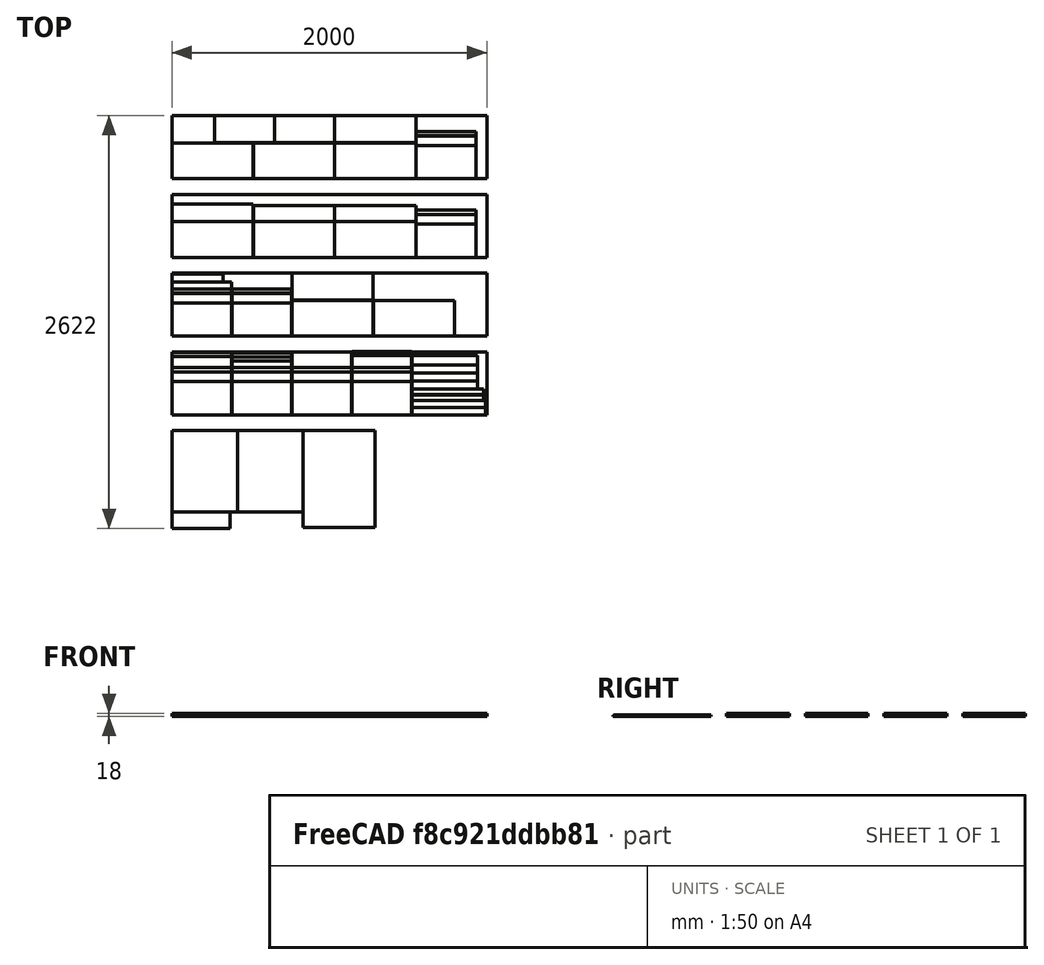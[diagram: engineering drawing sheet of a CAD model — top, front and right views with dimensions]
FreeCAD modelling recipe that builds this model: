
FCSTD DOCUMENT  (FreeCAD 0.16R)
Label: Schnittplan
License: All rights reserved
LicenseURL: http://en.wikipedia.org/wiki/All_rights_reserved
objects: Part::Box×66, App::DocumentObjectGroup×23
note: 66 computed .brp shape members not serialized (recipe doc carries the construction recipe); baked Part::Feature solids carry a one-line shape summary decoded from their .brp

FEATURE [Part::Box] Box  label="BRETT"
  Height = 18
  Length = 2000
  Width = 400
FEATURE [Part::Box] Box001  label="Dach Front Big"
  Height = 18
  Length = 380
  Placement = pos=(0,300,0) rot=(0,0,1;0rad)
  Width = 70
FEATURE [Part::Box] Box002  label="Dach Back small"
  Height = 18
  Length = 380
  Placement = pos=(381,300,0) rot=(0,0,1;0rad)
  Width = 40
FEATURE [Part::Box] Box003  label="Zarge Back outer upper"
  Height = 18
  Length = 380
  Placement = pos=(1143,211,0) rot=(0,0,1;0rad)
  Width = 60
FEATURE [Part::Box] Box004  label="Zarge Back outer lower "
  Height = 18
  Length = 380
  Placement = pos=(1143,272,0) rot=(0,0,1;0rad)
  Width = 27
FEATURE [Part::Box] Box005  label="Zarge Front inner"
  Height = 18
  Length = 380
  Placement = pos=(1143,0,0) rot=(0,0,1;0rad)
  Width = 210
FEATURE [Part::Box] Box007  label="Zarge Front outer lower"
  Height = 18
  Length = 380
  Placement = pos=(762,272,0) rot=(0,0,1;0rad)
  Width = 27
FEATURE [Part::Box] Box008  label="Zarge Back inner"
  Height = 18
  Length = 380
  Placement = pos=(762,0,0) rot=(0,0,1;0rad)
  Width = 210
FEATURE [Part::Box] Box006  label="Zarge Front outer upper"
  Height = 18
  Length = 380
  Placement = pos=(762,211,0) rot=(0,0,1;0rad)
  Width = 60
FEATURE [Part::Box] Box009  label="Boden Back with Hole"
  Height = 18
  Length = 380
  Placement = pos=(762,300,0) rot=(0,0,1;0rad)
  Width = 100
FEATURE [Part::Box] Box010  label="Boden Flogloch outer upper"
  Height = 18
  Length = 380
  Placement = pos=(1143,300,0) rot=(0,0,1;0rad)
  Width = 75
FEATURE [Part::Box] Box014  label="Zarge Front outer lower001"
  Height = 18
  Length = 380
  Placement = pos=(0,272,0) rot=(0,0,1;0rad)
  Width = 27
FEATURE [Part::Box] Box015  label="Zarge Back inner001"
  Height = 18
  Length = 380
  Placement = pos=(381,0,0) rot=(0,0,1;0rad)
  Width = 210
FEATURE [Part::Box] Box016  label="Zarge Front outer upper001"
  Height = 18
  Length = 380
  Placement = pos=(0,211,0) rot=(0,0,1;0rad)
  Width = 60
FEATURE [Part::Box] Box012  label="Zarge Back outer lower 001"
  Height = 18
  Length = 380
  Placement = pos=(381,272,0) rot=(0,0,1;0rad)
  Width = 27
FEATURE [Part::Box] Box013  label="Zarge Front inner001"
  Height = 18
  Length = 380
  Width = 210
FEATURE [Part::Box] Box017  label="Boden Fluglochverschluss"
  Height = 18
  Length = 380
  Placement = pos=(381,367,0) rot=(0,0,1;0rad)
  Width = 25
FEATURE [Part::Box] Box018  label="Boden Fluglochverschluss001"
  Height = 18
  Length = 380
  Placement = pos=(381,341,0) rot=(0,0,1;0rad)
  Width = 25
FEATURE [Part::Box] Box019  label="Boden Fluglochverschluss002"
  Height = 18
  Length = 380
  Placement = pos=(0,371,0) rot=(0,0,1;0rad)
  Width = 25
FEATURE [Part::Box] Box011  label="Zarge Back outer upper001"
  Height = 18
  Length = 380
  Placement = pos=(381,211,0) rot=(0,0,1;0rad)
  Width = 60
FEATURE [Part::Box] Box020  label="Boden Fluglochverschluss003"
  Height = 18
  Length = 380
  Placement = pos=(1143,376,0) rot=(0,0,1;0rad)
  Width = 25
FEATURE [Part::Box] Box021  label="Boden Seite rechts unten"
  Height = 18
  Length = 466
  Placement = pos=(1524,0,0) rot=(0,0,1;0rad)
  Width = 45
FEATURE [App::DocumentObjectGroup] Gruppe014  label="Gruppe 380 Zarge"
  Group = -> [Box003,Box004,Box005,Box007,Box008,Box006]
FEATURE [App::DocumentObjectGroup] Gruppe016  label="Gruppe 380 Zarge2"
  Group = -> [Box012,Box013,Box014,Box015,Box016,Box011]
FEATURE [Part::Box] Box022  label="BRETT2"
  Height = 18
  Length = 2000
  Placement = pos=(0,500,0) rot=(0,0,1;0rad)
  Width = 400
FEATURE [Part::Box] Box023  label="Boden Seite links unten"
  Height = 18
  Length = 466
  Placement = pos=(1524,46,0) rot=(0,0,1;0rad)
  Width = 45
FEATURE [App::DocumentObjectGroup] Gruppe009  label="Gruppe 466"
  Group = -> [Box021,Box023]
FEATURE [Part::Box] Box024  label="Boden Seite rechts oben"
  Height = 18
  Length = 456
  Placement = pos=(1524,92,0) rot=(0,0,1;0rad)
  Width = 35
FEATURE [Part::Box] Box025  label="Boden Seite links oben"
  Height = 18
  Length = 456
  Placement = pos=(1524,128,0) rot=(0,0,1;0rad)
  Width = 35
FEATURE [App::DocumentObjectGroup] Gruppe008  label="Gruppe 456"
  Group = -> [Box024,Box025]
FEATURE [Part::Box] Box026  label="Boden fuß vorne"
  Height = 18
  Length = 416
  Placement = pos=(1524,215,0) rot=(0,0,1;0rad)
  Width = 50
FEATURE [Part::Box] Box027  label="Boden fuß hinten unten"
  Height = 18
  Length = 416
  Placement = pos=(1524,164,0) rot=(0,0,1;0rad)
  Width = 50
FEATURE [Part::Box] Box028  label="Boden fuß hinten oben"
  Height = 18
  Length = 416
  Placement = pos=(1524,266,0) rot=(0,0,1;0rad)
  Width = 50
FEATURE [Part::Box] Box029  label="Boden Anflugbrett"
  Height = 18
  Length = 416
  Placement = pos=(1524,317,0) rot=(0,0,1;0rad)
  Width = 60
FEATURE [App::DocumentObjectGroup] Gruppe006  label="Gruppe 416"
  Group = -> [Box026,Box027,Box028,Box029]
FEATURE [Part::Box] Box030  label="Boden Varroalade Griff"
  Height = 18
  Length = 346
  Placement = pos=(1524,378,0) rot=(0,0,1;0rad)
  Width = 18
FEATURE [App::DocumentObjectGroup] Gruppe007  label="Gruppe 346"
  Group = -> [Box030]
FEATURE [Part::Box] Box035  label="Zarge Front inner002"
  Height = 18
  Length = 380
  Placement = pos=(0,500,0) rot=(0,0,1;0rad)
  Width = 210
FEATURE [Part::Box] Box032  label="Zarge Back inner002"
  Height = 18
  Length = 380
  Placement = pos=(381,500,0) rot=(0,0,1;0rad)
  Width = 210
FEATURE [Part::Box] Box031  label="Zarge Front outer lower002"
  Height = 18
  Length = 380
  Placement = pos=(0,772,0) rot=(0,0,1;0rad)
  Width = 27
FEATURE [Part::Box] Box034  label="Zarge Back outer lower 002"
  Height = 18
  Length = 380
  Placement = pos=(381,772,0) rot=(0,0,1;0rad)
  Width = 27
FEATURE [Part::Box] Box033  label="Zarge Front outer upper002"
  Height = 18
  Length = 380
  Placement = pos=(0,711,0) rot=(0,0,1;0rad)
  Width = 60
FEATURE [Part::Box] Box036  label="Zarge Back outer upper002"
  Height = 18
  Length = 380
  Placement = pos=(381,711,0) rot=(0,0,1;0rad)
  Width = 60
FEATURE [App::DocumentObjectGroup] Gruppe020  label="Gruppe 380 Zarge003"
  Group = -> [Box034,Box035,Box031,Box032,Box033,Box036]
FEATURE [Part::Box] Box037  label="Zarge Front inner003"
  Height = 18
  Length = 380
  Placement = pos=(1551,1500,0) rot=(0,0,1;0rad)
  Width = 210
FEATURE [Part::Box] Box038  label="Zarge Back inner003"
  Height = 18
  Length = 380
  Placement = pos=(1551,1000,0) rot=(0,0,1;0rad)
  Width = 210
FEATURE [Part::Box] Box039  label="Zarge Front outer lower003"
  Height = 18
  Length = 380
  Placement = pos=(1551,1772,0) rot=(0,0,1;0rad)
  Width = 27
FEATURE [Part::Box] Box040  label="Zarge Back outer lower 003"
  Height = 18
  Length = 380
  Placement = pos=(1551,1272,0) rot=(0,0,1;0rad)
  Width = 27
FEATURE [Part::Box] Box041  label="Zarge Front outer upper003"
  Height = 18
  Length = 380
  Placement = pos=(1551,1711,0) rot=(0,0,1;0rad)
  Width = 60
FEATURE [Part::Box] Box042  label="Zarge Back outer upper003"
  Height = 18
  Length = 380
  Placement = pos=(1551,1211,0) rot=(0,0,1;0rad)
  Width = 60
FEATURE [App::DocumentObjectGroup] Gruppe023  label="Gruppe 380 Zarge004"
  Group = -> [Box040,Box037,Box039,Box038,Box041,Box042]
FEATURE [Part::Box] Box043  label="BRETT 3"
  Height = 18
  Length = 2000
  Placement = pos=(0,1000,0) rot=(0,0,1;0rad)
  Width = 400
FEATURE [Part::Box] Box044  label="Zarge 1 Links"
  Height = 18
  Length = 516
  Placement = pos=(0,1000,0) rot=(0,0,1;0rad)
  Width = 227
FEATURE [Part::Box] Box045  label="Zarge 1 Rechts"
  Height = 18
  Length = 516
  Placement = pos=(517,1000,0) rot=(0,0,1;0rad)
  Width = 227
FEATURE [App::DocumentObjectGroup] Gruppe012  label="Gruppe 516 Zarge "
  Group = -> [Box044,Box045]
FEATURE [App::DocumentObjectGroup] Gruppe002  label="Zarge1"
  Group = -> [Gruppe012,Gruppe014]
FEATURE [Part::Box] Box046  label="Zarge 1 Links001"
  Height = 18
  Length = 516
  Placement = pos=(0,1500,0) rot=(0,0,1;0rad)
  Width = 227
FEATURE [Part::Box] Box047  label="Zarge 1 Rechts001"
  Height = 18
  Length = 516
  Placement = pos=(1034,1000,0) rot=(0,0,1;0rad)
  Width = 227
FEATURE [App::DocumentObjectGroup] Gruppe013  label="Gruppe 516 Zarge 2"
  Group = -> [Box047,Box046]
FEATURE [App::DocumentObjectGroup] Gruppe004  label="Zarge2"
  Group = -> [Gruppe013,Gruppe016]
FEATURE [Part::Box] Box048  label="BRETT 4"
  Height = 18
  Length = 2000
  Placement = pos=(0,1500,0) rot=(0,0,1;0rad)
  Width = 400
FEATURE [App::DocumentObjectGroup] Gruppe  label="Bretter"
  Group = -> [Box,Box022,Box043,Box048]
FEATURE [Part::Box] Box049  label="Zarge 1 Rechts002"
  Height = 18
  Length = 516
  Placement = pos=(1034,1500,0) rot=(0,0,1;0rad)
  Width = 227
FEATURE [Part::Box] Box050  label="Zarge 1 Links002"
  Height = 18
  Length = 516
  Placement = pos=(517,1500,0) rot=(0,0,1;0rad)
  Width = 227
FEATURE [App::DocumentObjectGroup] Gruppe019  label="Gruppe 516 Zarge 003"
  Group = -> [Box049,Box050]
FEATURE [App::DocumentObjectGroup] Gruppe018  label="Zarge3"
  Group = -> [Gruppe019,Gruppe020]
FEATURE [Part::Box] Box051  label="Boden Flogloch inner lower"
  Height = 18
  Length = 380
  Placement = pos=(0,800,0) rot=(0,0,1;0rad)
  Width = 42
FEATURE [App::DocumentObjectGroup] Gruppe005  label="Gruppe 380"
  Group = -> [Box009,Box010,Box017,Box018,Box019,Box020,Box051]
FEATURE [Part::Box] Box052  label="Dach Seitenteile"
  Height = 18
  Length = 516
  Placement = pos=(0,1228,0) rot=(0,0,1;0rad)
  Width = 110
FEATURE [Part::Box] Box053  label="Boden Seite links"
  Height = 18
  Length = 516
  Placement = pos=(517,1228,0) rot=(0,0,1;0rad)
  Width = 100
FEATURE [Part::Box] Box054  label="Boden Seite rechts"
  Height = 18
  Length = 516
  Placement = pos=(1034,1228,0) rot=(0,0,1;0rad)
  Width = 100
FEATURE [App::DocumentObjectGroup] Gruppe010  label="Gruppe 516"
  Group = -> [Box053,Box054]
FEATURE [Part::Box] Box055  label="Boden unter Anflugbrett"
  Height = 18
  Length = 326
  Placement = pos=(0,843,0) rot=(0,0,1;0rad)
  Width = 50
FEATURE [App::DocumentObjectGroup] Gruppe011  label="Gruppe 326"
  Group = -> [Box055]
FEATURE [Part::Box] Box056  label="Zarge 1 Rechts003"
  Height = 18
  Length = 516
  Placement = pos=(762,500,0) rot=(0,0,1;0rad)
  Width = 227
FEATURE [Part::Box] Box060  label="Futterzarge Rechts"
  Height = 18
  Length = 516
  Placement = pos=(762,728,0) rot=(0,0,1;0rad)
  Width = 172
FEATURE [Part::Box] Box061  label="Futterzarge Links"
  Height = 18
  Length = 516
  Placement = pos=(1034,1728,0) rot=(0,0,1;0rad)
  Width = 172
FEATURE [Part::Box] Box062  label="Futterzarge Front"
  Height = 18
  Length = 380
  Placement = pos=(653,1728,0) rot=(0,0,1;0rad)
  Width = 172
FEATURE [Part::Box] Box063  label="Futterzarge hinten"
  Height = 18
  Length = 380
  Placement = pos=(272,1728,0) rot=(0,0,1;0rad)
  Width = 172
FEATURE [Part::Box] Box064  label=" Dach Unterseite Sperrholz"
  Height = 8
  Length = 416
  Placement = pos=(0,-616,0) rot=(0,0,1;0rad)
  Width = 516
FEATURE [Part::Box] Box065  label=" Dach Dach Material Wasserbeständig"
  Height = 8
  Length = 457
  Placement = pos=(834,-715,0) rot=(0,0,1;0rad)
  Width = 615
FEATURE [App::DocumentObjectGroup] Gruppe003  label="Dach"
  Group = -> [Box001,Box002,Box052,Box064,Box065]
FEATURE [Part::Box] Box066  label=" Futterzarge Unterseite Sperrholz"
  Height = 8
  Length = 416
  Placement = pos=(417,-616,0) rot=(0,0,1;0rad)
  Width = 516
FEATURE [App::DocumentObjectGroup] Gruppe026  label="Futterzarge"
  Group = -> [Box060,Box061,Box062,Box063,Box066]
FEATURE [Part::Box] Box067  label="Bearbeitungsloch Deckel"
  Height = 5
  Length = 370
  Placement = pos=(0,-722,0) rot=(0,0,1;0rad)
  Width = 105
FEATURE [App::DocumentObjectGroup] Gruppe001  label="Boden"
  Group = -> [Gruppe005,Gruppe006,Gruppe007,Gruppe008,Gruppe009,Gruppe010,Gruppe011,Box067]
FEATURE [Part::Box] Box068  label="Zarge 1 Rechts004"
  Height = 18
  Length = 516
  Placement = pos=(1279,500,0) rot=(0,0,1;0rad)
  Width = 227
FEATURE [App::DocumentObjectGroup] Gruppe022  label="Gruppe 516 Zarge 004"
  Group = -> [Box056,Box068]
FEATURE [App::DocumentObjectGroup] Gruppe021  label="Zarge4"
  Group = -> [Gruppe022,Gruppe023]
